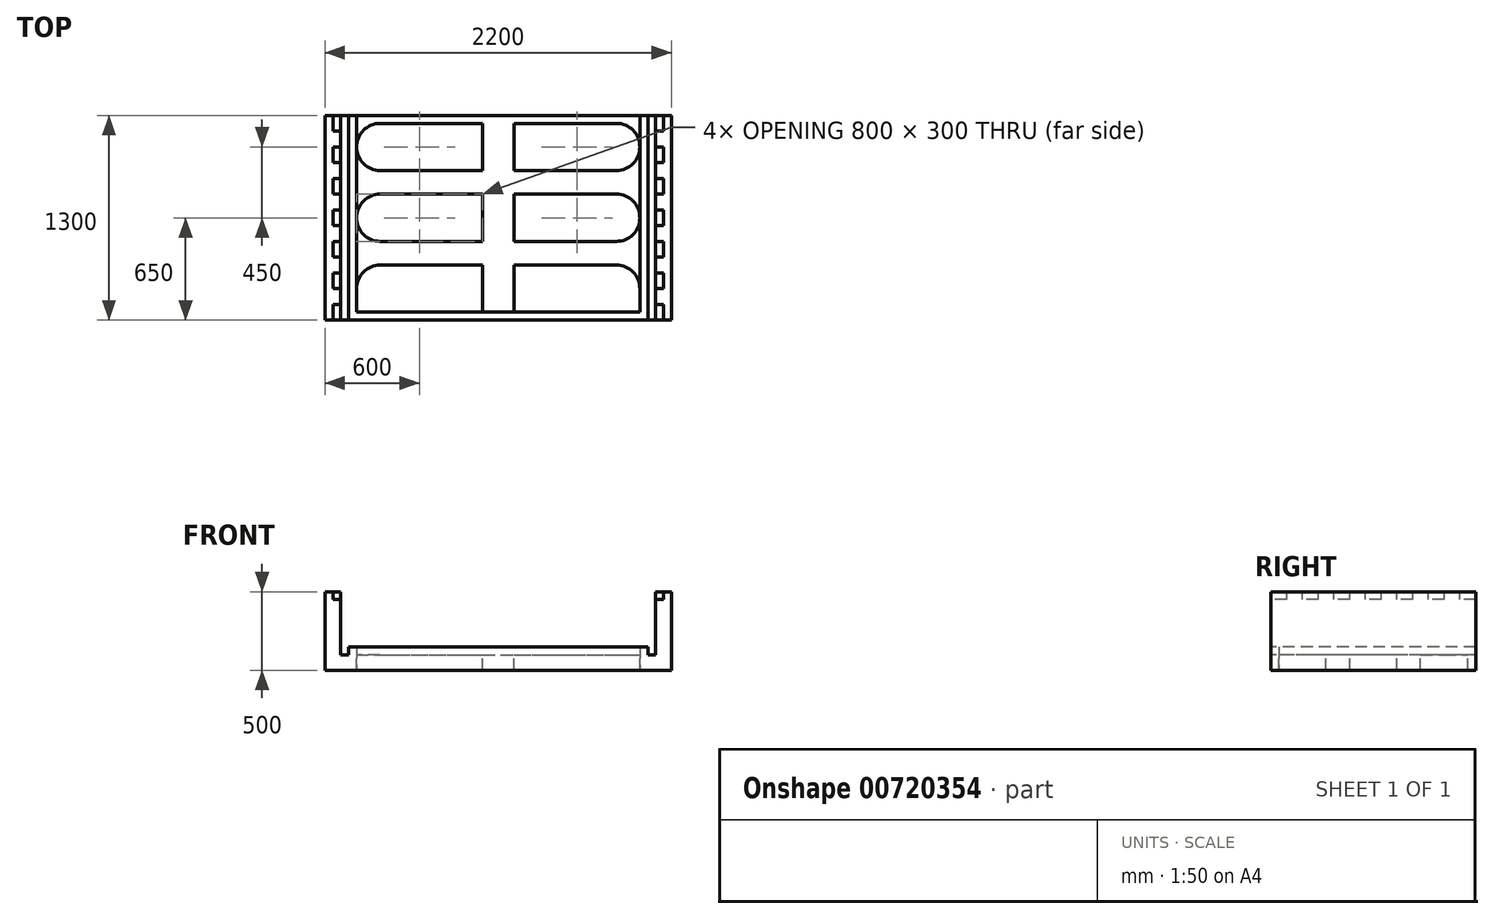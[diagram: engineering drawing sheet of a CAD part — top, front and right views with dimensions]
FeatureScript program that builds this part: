
annotation { "Feature Type Name" : "Feature", "Feature Type Description" : "" }
export const myFeature = defineFeature(function(context is Context, id is Id, definition is map)
    precondition{}
    {
        {
            var Q0;
            Q0=qCreatedBy(makeId("Top.planeOp"),FACE);
            var sketch = newSketch(context, id + "F0", { "sketchPlane" : qUnion([Q0])});
            skLineSegment(sketch, "E0.bottom", {"start": v(1100, 650) * mm, "end": v(-1100, 650) * mm});
            skLineSegment(sketch, "E0.top", {"start": v(1100, -650) * mm, "end": v(-1100, -650) * mm});
            skLineSegment(sketch, "E0.left", {"start": v(1100, 650) * mm, "end": v(1100, -650) * mm});
            skLineSegment(sketch, "E0.right", {"start": v(-1100, 650) * mm, "end": v(-1100, -650) * mm});
            skPoint(sketch, "E0.middle", {"position": v(0, 0) * mm});
            skSolve(sketch);
        }
        {
            var Q0;
            Q0=makeQuery(id+"F0.imprint","IMPRINT",FACE,{"disambiguationData":[TD([[makeQuery(id+"F0.imprint","IMPRINT",EDGE,{"derivedFrom":sQuery(id+"F0.wireOp",EDGE,"E0.bottom")}),1.0]])]});
            extrude(context, id + "F1", {"entities" : qUnion([Q0]), "oppositeDirection" : true, "depth" : 500 * mm, "offsetDistance" : 25 * mm});
        }
        {
            var Q0;
            Q0=makeQuery(id+"F1.opExtrude","SWEPT_FACE",FACE,{"disambiguationData":[OSD([sQuery(id+"F0.wireOp",EDGE,"E0.top")])]});
            var sketch = newSketch(context, id + "F2", { "sketchPlane" : qUnion([Q0])});
            skLineSegment(sketch, "E1.bottom", {"start": v(-1000, 0) * mm, "end": v(1000, 0) * mm});
            skLineSegment(sketch, "E1.top", {"start": v(-1000, -400) * mm, "end": v(1000, -400) * mm});
            skLineSegment(sketch, "E1.left", {"start": v(-1000, 0) * mm, "end": v(-1000, -400) * mm});
            skLineSegment(sketch, "E1.right", {"start": v(1000, 0) * mm, "end": v(1000, -400) * mm});
            skSolve(sketch);
        }
        {
            var Q0;
            Q0=makeQuery(id+"F2.imprint","IMPRINT",FACE,{"disambiguationData":[TD([[makeQuery(id+"F2.imprint","IMPRINT",EDGE,{"derivedFrom":sQuery(id+"F2.wireOp",EDGE,"E1.bottom")}),1.0]])]});
            extrude(context, id + "F3", {"entities" : qUnion([Q0]), "operationType" : NewBodyOperationType.REMOVE, "oppositeDirection" : true, "depth" : 1300 * mm, "offsetDistance" : 25 * mm});
        }
        {
            var Q0;
            {var subQ0=sQuery(id+"F0.wireOp",EDGE,"E0.bottom");var subQ1=sQuery(id+"F0.wireOp",EDGE,"E0.right");var subQ2=sQuery(id+"F0.wireOp",EDGE,"E0.top");Q0=makeQuery(id+"F3.boolean.opBoolean","SPLIT",FACE,{"disambiguationData":[TD([makeQuery(id+"F1.opExtrude","SWEPT_FACE",FACE,{"disambiguationData":[OSD([subQ1])]})])],"derivedFrom":makeQuery(id+"F1.opExtrude","CAP_FACE",FACE,{"disambiguationData":[OSD([subQ0,subQ2,sQuery(id+"F0.wireOp",EDGE,"E0.left"),subQ1])],"isStart":true})});}
            var sketch = newSketch(context, id + "F4", { "sketchPlane" : qUnion([Q0])});
            skLineSegment(sketch, "E2", {"start": v(-1050, 650) * mm, "end": v(-1050, -650) * mm});
            skLineSegment(sketch, "E3", {"start": v(-1050, -550) * mm, "end": v(-1000, -550) * mm});
            skLineSegment(sketch, "E4", {"start": v(-1050, -450) * mm, "end": v(-1000, -450) * mm});
            skLineSegment(sketch, "E5", {"start": v(-1050, -350) * mm, "end": v(-1000, -350) * mm});
            skLineSegment(sketch, "E6", {"start": v(-1050, -250) * mm, "end": v(-1000, -250) * mm});
            skLineSegment(sketch, "E7", {"start": v(-1050, -150) * mm, "end": v(-1000, -150) * mm});
            skLineSegment(sketch, "E8", {"start": v(-1050, -50) * mm, "end": v(-1000, -50) * mm});
            skLineSegment(sketch, "E9", {"start": v(-1050, 50) * mm, "end": v(-1000, 50) * mm});
            skLineSegment(sketch, "E10", {"start": v(-1050, 150) * mm, "end": v(-1000, 150) * mm});
            skLineSegment(sketch, "E11", {"start": v(-1050, 250) * mm, "end": v(-1000, 250) * mm});
            skLineSegment(sketch, "E12", {"start": v(-1050, 350) * mm, "end": v(-1000, 350) * mm});
            skLineSegment(sketch, "E13", {"start": v(-1050, 450) * mm, "end": v(-1000, 450) * mm});
            skLineSegment(sketch, "E14", {"start": v(-1050, 550) * mm, "end": v(-1000, 550) * mm});
            skSolve(sketch);
        }
        {
            var Q0;
            {var subQ6=sQuery(id+"F4.wireOp",EDGE,"E3");Q0=makeQuery(id+"F4.imprint","IMPRINT",FACE,{"disambiguationData":[TD([[makeQuery(id+"F4.imprint","IMPRINT",EDGE,{"derivedFrom":subQ6}),-1.0]])]});}
            var Q1;
            {var subQ0=sQuery(id+"F4.wireOp",EDGE,"E4");Q1=makeQuery(id+"F4.imprint","IMPRINT",FACE,{"disambiguationData":[TD([[makeQuery(id+"F4.imprint","IMPRINT",EDGE,{"derivedFrom":subQ0}),1.0]])]});}
            var Q2;
            {var subQ0=sQuery(id+"F4.wireOp",EDGE,"E6");Q2=makeQuery(id+"F4.imprint","IMPRINT",FACE,{"disambiguationData":[TD([[makeQuery(id+"F4.imprint","IMPRINT",EDGE,{"derivedFrom":subQ0}),1.0]])]});}
            var Q3;
            {var subQ0=sQuery(id+"F4.wireOp",EDGE,"E8");Q3=makeQuery(id+"F4.imprint","IMPRINT",FACE,{"disambiguationData":[TD([[makeQuery(id+"F4.imprint","IMPRINT",EDGE,{"derivedFrom":subQ0}),1.0]])]});}
            var Q4;
            {var subQ0=sQuery(id+"F4.wireOp",EDGE,"E10");Q4=makeQuery(id+"F4.imprint","IMPRINT",FACE,{"disambiguationData":[TD([[makeQuery(id+"F4.imprint","IMPRINT",EDGE,{"derivedFrom":subQ0}),1.0]])]});}
            var Q5;
            {var subQ0=sQuery(id+"F4.wireOp",EDGE,"E12");Q5=makeQuery(id+"F4.imprint","IMPRINT",FACE,{"disambiguationData":[TD([[makeQuery(id+"F4.imprint","IMPRINT",EDGE,{"derivedFrom":subQ0}),1.0]])]});}
            var Q6;
            {var subQ7=sQuery(id+"F4.wireOp",EDGE,"E14");Q6=makeQuery(id+"F4.imprint","IMPRINT",FACE,{"disambiguationData":[TD([[makeQuery(id+"F4.imprint","IMPRINT",EDGE,{"derivedFrom":subQ7}),1.0]])]});}
            extrude(context, id + "F5", {"entities" : qUnion([Q0, Q1, Q2, Q3, Q4, Q5, Q6]), "operationType" : NewBodyOperationType.REMOVE, "oppositeDirection" : true, "depth" : 50 * mm, "offsetDistance" : 25 * mm});
        }
        {
            var Q0;
            {var subQ0=sQuery(id+"F0.wireOp",EDGE,"E0.bottom");var subQ1=sQuery(id+"F0.wireOp",EDGE,"E0.top");var subQ2=sQuery(id+"F0.wireOp",EDGE,"E0.left");Q0=makeQuery(id+"F3.boolean.opBoolean","SPLIT",FACE,{"disambiguationData":[TD([makeQuery(id+"F1.opExtrude","SWEPT_FACE",FACE,{"disambiguationData":[OSD([subQ2])]})])],"derivedFrom":makeQuery(id+"F1.opExtrude","CAP_FACE",FACE,{"disambiguationData":[OSD([subQ0,subQ1,subQ2,sQuery(id+"F0.wireOp",EDGE,"E0.right")])],"isStart":true})});}
            var sketch = newSketch(context, id + "F6", { "sketchPlane" : qUnion([Q0])});
            skLineSegment(sketch, "E15", {"start": v(1050, -650) * mm, "end": v(1050, 650) * mm});
            skLineSegment(sketch, "E16", {"start": v(1000, -550) * mm, "end": v(1050, -550) * mm});
            skLineSegment(sketch, "E17", {"start": v(1000, -450) * mm, "end": v(1050, -450) * mm});
            skLineSegment(sketch, "E18", {"start": v(1000, -350) * mm, "end": v(1050, -350) * mm});
            skLineSegment(sketch, "E19", {"start": v(1000, -250) * mm, "end": v(1050, -250) * mm});
            skLineSegment(sketch, "E20", {"start": v(1000, -150) * mm, "end": v(1050, -150) * mm});
            skLineSegment(sketch, "E21", {"start": v(1000, -50) * mm, "end": v(1050, -50) * mm});
            skLineSegment(sketch, "E22", {"start": v(1000, 50) * mm, "end": v(1050, 50) * mm});
            skLineSegment(sketch, "E23", {"start": v(1000, 150) * mm, "end": v(1050, 150) * mm});
            skLineSegment(sketch, "E24", {"start": v(1000, 250) * mm, "end": v(1050, 250) * mm});
            skLineSegment(sketch, "E25", {"start": v(1000, 350) * mm, "end": v(1050, 350) * mm});
            skLineSegment(sketch, "E26", {"start": v(1000, 450) * mm, "end": v(1050, 450) * mm});
            skLineSegment(sketch, "E27", {"start": v(1000, 550) * mm, "end": v(1050, 550) * mm});
            skSolve(sketch);
        }
        {
            var Q0;
            {var subQ7=sQuery(id+"F6.wireOp",EDGE,"E27");Q0=makeQuery(id+"F6.imprint","IMPRINT",FACE,{"disambiguationData":[TD([[makeQuery(id+"F6.imprint","IMPRINT",EDGE,{"derivedFrom":subQ7}),1.0]])]});}
            var Q1;
            {var subQ0=sQuery(id+"F6.wireOp",EDGE,"E25");Q1=makeQuery(id+"F6.imprint","IMPRINT",FACE,{"disambiguationData":[TD([[makeQuery(id+"F6.imprint","IMPRINT",EDGE,{"derivedFrom":subQ0}),1.0]])]});}
            var Q2;
            {var subQ0=sQuery(id+"F6.wireOp",EDGE,"E23");Q2=makeQuery(id+"F6.imprint","IMPRINT",FACE,{"disambiguationData":[TD([[makeQuery(id+"F6.imprint","IMPRINT",EDGE,{"derivedFrom":subQ0}),1.0]])]});}
            var Q3;
            {var subQ0=sQuery(id+"F6.wireOp",EDGE,"E21");Q3=makeQuery(id+"F6.imprint","IMPRINT",FACE,{"disambiguationData":[TD([[makeQuery(id+"F6.imprint","IMPRINT",EDGE,{"derivedFrom":subQ0}),1.0]])]});}
            var Q4;
            {var subQ0=sQuery(id+"F6.wireOp",EDGE,"E19");Q4=makeQuery(id+"F6.imprint","IMPRINT",FACE,{"disambiguationData":[TD([[makeQuery(id+"F6.imprint","IMPRINT",EDGE,{"derivedFrom":subQ0}),1.0]])]});}
            var Q5;
            {var subQ0=sQuery(id+"F6.wireOp",EDGE,"E17");Q5=makeQuery(id+"F6.imprint","IMPRINT",FACE,{"disambiguationData":[TD([[makeQuery(id+"F6.imprint","IMPRINT",EDGE,{"derivedFrom":subQ0}),1.0]])]});}
            var Q6;
            {var subQ6=sQuery(id+"F6.wireOp",EDGE,"E16");Q6=makeQuery(id+"F6.imprint","IMPRINT",FACE,{"disambiguationData":[TD([[makeQuery(id+"F6.imprint","IMPRINT",EDGE,{"derivedFrom":subQ6}),-1.0]])]});}
            extrude(context, id + "F7", {"entities" : qUnion([Q0, Q1, Q2, Q3, Q4, Q5, Q6]), "operationType" : NewBodyOperationType.REMOVE, "oppositeDirection" : true, "depth" : 50 * mm, "offsetDistance" : 25 * mm});
        }
        {
            var Q0;
            Q0=makeQuery(id+"F3.boolean.opBoolean","COPY",FACE,{"derivedFrom":makeQuery(id+"F3.opExtrude","SWEPT_FACE",FACE,{"disambiguationData":[OSD([sQuery(id+"F2.wireOp",EDGE,"E1.top")])]})});
            var sketch = newSketch(context, id + "F8", { "sketchPlane" : qUnion([Q0])});
            skLineSegment(sketch, "E28.bottom", {"start": v(-950, 650) * mm, "end": v(950, 650) * mm});
            skLineSegment(sketch, "E28.top", {"start": v(-950, -650) * mm, "end": v(950, -650) * mm});
            skLineSegment(sketch, "E28.left", {"start": v(-950, 650) * mm, "end": v(-950, -650) * mm});
            skLineSegment(sketch, "E28.right", {"start": v(950, 650) * mm, "end": v(950, -650) * mm});
            skLineSegment(sketch, "E29", {"start": v(-900, 650) * mm, "end": v(-900, -650) * mm});
            skLineSegment(sketch, "E30", {"start": v(900, 650) * mm, "end": v(900, -650) * mm});
            skSolve(sketch);
        }
        {
            var Q0;
            {var subQ0=sQuery(id+"F8.wireOp",EDGE,"E28.left");Q0=makeQuery(id+"F8.imprint","IMPRINT",FACE,{"disambiguationData":[TD([[makeQuery(id+"F8.imprint","IMPRINT",EDGE,{"derivedFrom":subQ0}),1.0]])]});}
            var Q1;
            {var subQ0=sQuery(id+"F8.wireOp",EDGE,"E28.right");Q1=makeQuery(id+"F8.imprint","IMPRINT",FACE,{"disambiguationData":[TD([[makeQuery(id+"F8.imprint","IMPRINT",EDGE,{"derivedFrom":subQ0}),-1.0]])]});}
            extrude(context, id + "F9", {"entities" : qUnion([Q0, Q1]), "operationType" : NewBodyOperationType.ADD, "depth" : 50 * mm, "offsetDistance" : 25 * mm});
        }
        {
            var Q0;
            {var subQ2=sQuery(id+"F2.wireOp",EDGE,"E1.top");var subQ6=sQuery(id+"F8.wireOp",EDGE,"E29");Q0=makeQuery(id+"F9.boolean.opBoolean","SPLIT",FACE,{"disambiguationData":[TD([makeQuery(id+"F9.opExtrude","SWEPT_FACE",FACE,{"disambiguationData":[OSD([subQ6])]})])],"derivedFrom":makeQuery(id+"F3.boolean.opBoolean","COPY",FACE,{"derivedFrom":makeQuery(id+"F3.opExtrude","SWEPT_FACE",FACE,{"disambiguationData":[OSD([subQ2])]})})});}
            var sketch = newSketch(context, id + "F10", { "sketchPlane" : qUnion([Q0])});
            skLineSegment(sketch, "E31", {"start": v(-900, -600) * mm, "end": v(900, -600) * mm});
            skSolve(sketch);
        }
        {
            var Q0;
            {var subQ0=sQuery(id+"F10.wireOp",EDGE,"E31");Q0=makeQuery(id+"F10.imprint","IMPRINT",FACE,{"disambiguationData":[TD([[makeQuery(id+"F10.imprint","IMPRINT",EDGE,{"derivedFrom":subQ0}),-1.0]])]});}
            extrude(context, id + "F11", {"entities" : qUnion([Q0]), "operationType" : NewBodyOperationType.ADD, "depth" : 50 * mm, "offsetDistance" : 25 * mm});
        }
        {
            var Q0;
            {var subQ2=sQuery(id+"F2.wireOp",EDGE,"E1.top");var subQ6=sQuery(id+"F8.wireOp",EDGE,"E29");Q0=makeQuery(id+"F9.boolean.opBoolean","SPLIT",FACE,{"disambiguationData":[TD([makeQuery(id+"F9.opExtrude","SWEPT_FACE",FACE,{"disambiguationData":[OSD([subQ6])]})])],"derivedFrom":makeQuery(id+"F3.boolean.opBoolean","COPY",FACE,{"derivedFrom":makeQuery(id+"F3.opExtrude","SWEPT_FACE",FACE,{"disambiguationData":[OSD([subQ2])]})})});}
            var sketch = newSketch(context, id + "F12", { "sketchPlane" : qUnion([Q0])});
            skLineSegment(sketch, "E32", {"start": v(-900, 600) * mm, "end": v(900, 600) * mm});
            skLineSegment(sketch, "E33.top", {"start": v(-900, 300) * mm, "end": v(900, 300) * mm});
            skLineSegment(sketch, "E33.left", {"start": v(-900, 600) * mm, "end": v(-900, 300) * mm});
            skLineSegment(sketch, "E33.right", {"start": v(900, 600) * mm, "end": v(900, 300) * mm});
            skLineSegment(sketch, "E34.bottom", {"start": v(-900, 150) * mm, "end": v(900, 150) * mm});
            skLineSegment(sketch, "E34.top", {"start": v(-900, -150) * mm, "end": v(900, -150) * mm});
            skLineSegment(sketch, "E34.left", {"start": v(-900, 150) * mm, "end": v(-900, -150) * mm});
            skLineSegment(sketch, "E34.right", {"start": v(900, 150) * mm, "end": v(900, -150) * mm});
            skLineSegment(sketch, "E35.bottom", {"start": v(-900, -600) * mm, "end": v(900, -600) * mm});
            skLineSegment(sketch, "E35.top", {"start": v(-900, -300) * mm, "end": v(900, -300) * mm});
            skLineSegment(sketch, "E35.left", {"start": v(-900, -600) * mm, "end": v(-900, -300) * mm});
            skLineSegment(sketch, "E35.right", {"start": v(900, -600) * mm, "end": v(900, -300) * mm});
            skLineSegment(sketch, "E36", {"start": v(0, 650) * mm, "end": v(0, -654.54) * mm});
            skPoint(sketch, "E36.endSnap0", {"position": v(0, -600) * mm});
            skLineSegment(sketch, "E37", {"start": v(-100, 650) * mm, "end": v(-100, -654.54) * mm});
            skLineSegment(sketch, "E38", {"start": v(100, 650) * mm, "end": v(100, -674.34) * mm});
            skSolve(sketch);
        }
        {
            var Q0;
            {var subQ0=sQuery(id+"F12.wireOp",EDGE,"E33.left");Q0=makeQuery(id+"F12.imprint","IMPRINT",FACE,{"disambiguationData":[TD([[makeQuery(id+"F12.imprint","IMPRINT",EDGE,{"derivedFrom":subQ0}),1.0]])]});}
            var Q1;
            {var subQ0=sQuery(id+"F12.wireOp",EDGE,"E33.right");Q1=makeQuery(id+"F12.imprint","IMPRINT",FACE,{"disambiguationData":[TD([[makeQuery(id+"F12.imprint","IMPRINT",EDGE,{"derivedFrom":subQ0}),-1.0]])]});}
            var Q2;
            {var subQ0=sQuery(id+"F12.wireOp",EDGE,"E34.right");Q2=makeQuery(id+"F12.imprint","IMPRINT",FACE,{"disambiguationData":[TD([[makeQuery(id+"F12.imprint","IMPRINT",EDGE,{"derivedFrom":subQ0}),-1.0]])]});}
            var Q3;
            {var subQ0=sQuery(id+"F12.wireOp",EDGE,"E34.left");Q3=makeQuery(id+"F12.imprint","IMPRINT",FACE,{"disambiguationData":[TD([[makeQuery(id+"F12.imprint","IMPRINT",EDGE,{"derivedFrom":subQ0}),1.0]])]});}
            var Q4;
            {var subQ0=sQuery(id+"F12.wireOp",EDGE,"E35.left");Q4=makeQuery(id+"F12.imprint","IMPRINT",FACE,{"disambiguationData":[TD([[makeQuery(id+"F12.imprint","IMPRINT",EDGE,{"derivedFrom":subQ0}),1.0]])]});}
            var Q5;
            {var subQ0=sQuery(id+"F12.wireOp",EDGE,"E35.right");Q5=makeQuery(id+"F12.imprint","IMPRINT",FACE,{"disambiguationData":[TD([[makeQuery(id+"F12.imprint","IMPRINT",EDGE,{"derivedFrom":subQ0}),-1.0]])]});}
            extrude(context, id + "F13", {"entities" : qUnion([Q0, Q1, Q2, Q3, Q4, Q5]), "operationType" : NewBodyOperationType.REMOVE, "oppositeDirection" : true, "depth" : 180 * mm, "offsetDistance" : 25 * mm});
        }
        {
            var Q0;
            Q0=makeQuery(id+"F13.boolean.opBoolean","COPY",EDGE,{"derivedFrom":makeQuery(id+"F13.opExtrude","SWEPT_EDGE",EDGE,{"disambiguationData":[OSD([sQuery(id+"F8.wireOp",EDGE,"E29"),sQuery(id+"F12.wireOp",EDGE,"E32"),sQuery(id+"F12.wireOp",EDGE,"E33.left")])]})});
            var Q1;
            Q1=makeQuery(id+"F13.boolean.opBoolean","COPY",EDGE,{"derivedFrom":makeQuery(id+"F13.opExtrude","SWEPT_EDGE",EDGE,{"disambiguationData":[OSD([sQuery(id+"F8.wireOp",EDGE,"E29"),sQuery(id+"F12.wireOp",EDGE,"E33.top"),sQuery(id+"F12.wireOp",EDGE,"E33.left")])]})});
            var Q2;
            Q2=makeQuery(id+"F13.boolean.opBoolean","COPY",EDGE,{"derivedFrom":makeQuery(id+"F13.opExtrude","SWEPT_EDGE",EDGE,{"disambiguationData":[OSD([sQuery(id+"F8.wireOp",EDGE,"E29"),sQuery(id+"F12.wireOp",EDGE,"E34.top"),sQuery(id+"F12.wireOp",EDGE,"E34.left")])]})});
            var Q3;
            Q3=makeQuery(id+"F13.boolean.opBoolean","COPY",EDGE,{"derivedFrom":makeQuery(id+"F13.opExtrude","SWEPT_EDGE",EDGE,{"disambiguationData":[OSD([sQuery(id+"F8.wireOp",EDGE,"E29"),sQuery(id+"F12.wireOp",EDGE,"E34.bottom"),sQuery(id+"F12.wireOp",EDGE,"E34.left")])]})});
            var Q4;
            Q4=makeQuery(id+"F13.boolean.opBoolean","MERGE",EDGE,{"derivedFrom":[makeQuery(id+"F11.opExtrude","SWEPT_EDGE",EDGE,{"disambiguationData":[OSD([sQuery(id+"F8.wireOp",EDGE,"E29"),sQuery(id+"F10.wireOp",EDGE,"E31")])]}),makeQuery(id+"F13.opExtrude","SWEPT_EDGE",EDGE,{"disambiguationData":[OSD([sQuery(id+"F12.wireOp",EDGE,"E35.bottom"),sQuery(id+"F12.wireOp",EDGE,"E35.left")])]})]});
            var Q5;
            Q5=makeQuery(id+"F13.boolean.opBoolean","COPY",EDGE,{"derivedFrom":makeQuery(id+"F13.opExtrude","SWEPT_EDGE",EDGE,{"disambiguationData":[OSD([sQuery(id+"F8.wireOp",EDGE,"E29"),sQuery(id+"F12.wireOp",EDGE,"E35.top"),sQuery(id+"F12.wireOp",EDGE,"E35.left")])]})});
            var Q6;
            Q6=makeQuery(id+"F13.boolean.opBoolean","COPY",EDGE,{"derivedFrom":makeQuery(id+"F13.opExtrude","SWEPT_EDGE",EDGE,{"disambiguationData":[OSD([sQuery(id+"F8.wireOp",EDGE,"E30"),sQuery(id+"F12.wireOp",EDGE,"E32"),sQuery(id+"F12.wireOp",EDGE,"E33.right")])]})});
            var Q7;
            Q7=makeQuery(id+"F13.boolean.opBoolean","COPY",EDGE,{"derivedFrom":makeQuery(id+"F13.opExtrude","SWEPT_EDGE",EDGE,{"disambiguationData":[OSD([sQuery(id+"F8.wireOp",EDGE,"E30"),sQuery(id+"F12.wireOp",EDGE,"E34.bottom"),sQuery(id+"F12.wireOp",EDGE,"E34.right")])]})});
            var Q8;
            Q8=makeQuery(id+"F13.boolean.opBoolean","COPY",EDGE,{"derivedFrom":makeQuery(id+"F13.opExtrude","SWEPT_EDGE",EDGE,{"disambiguationData":[OSD([sQuery(id+"F8.wireOp",EDGE,"E30"),sQuery(id+"F12.wireOp",EDGE,"E35.top"),sQuery(id+"F12.wireOp",EDGE,"E35.right")])]})});
            var Q9;
            Q9=makeQuery(id+"F13.boolean.opBoolean","COPY",EDGE,{"derivedFrom":makeQuery(id+"F13.opExtrude","SWEPT_EDGE",EDGE,{"disambiguationData":[OSD([sQuery(id+"F8.wireOp",EDGE,"E30"),sQuery(id+"F12.wireOp",EDGE,"E33.top"),sQuery(id+"F12.wireOp",EDGE,"E33.right")])]})});
            var Q10;
            Q10=makeQuery(id+"F13.boolean.opBoolean","COPY",EDGE,{"derivedFrom":makeQuery(id+"F13.opExtrude","SWEPT_EDGE",EDGE,{"disambiguationData":[OSD([sQuery(id+"F8.wireOp",EDGE,"E30"),sQuery(id+"F12.wireOp",EDGE,"E34.top"),sQuery(id+"F12.wireOp",EDGE,"E34.right")])]})});
            var Q11;
            Q11=makeQuery(id+"F13.boolean.opBoolean","MERGE",EDGE,{"derivedFrom":[makeQuery(id+"F11.opExtrude","SWEPT_EDGE",EDGE,{"disambiguationData":[OSD([sQuery(id+"F8.wireOp",EDGE,"E30"),sQuery(id+"F10.wireOp",EDGE,"E31")])]}),makeQuery(id+"F13.opExtrude","SWEPT_EDGE",EDGE,{"disambiguationData":[OSD([sQuery(id+"F12.wireOp",EDGE,"E35.bottom"),sQuery(id+"F12.wireOp",EDGE,"E35.right")])]})]});
            fillet(context, id + "F14", {"entities" : qUnion([Q0, Q1, Q2, Q3, Q4, Q5, Q6, Q7, Q8, Q9, Q10, Q11]), "radius" : 150 * mm, "tangentPropagation" : true, "allowEdgeOverflow" : false});
        }
    });
